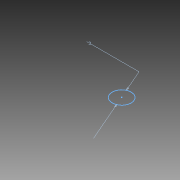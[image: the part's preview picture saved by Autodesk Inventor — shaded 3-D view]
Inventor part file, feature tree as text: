
AUTODESK INVENTOR PART (.ipt)
format: ipt  version: 2011 SP2 (Build 150309200, 309)  size: 59,392 bytes
history: native  units: mm
features: sketch x2
ambient origin geometry x8: Origin, YZ Plane, XZ Plane, XY Plane, X Axis, Y Axis, Z Axis, Center Point
feature tree (2):
  sketch  "Sketch1"
  sketch  "3D Sketch1"
